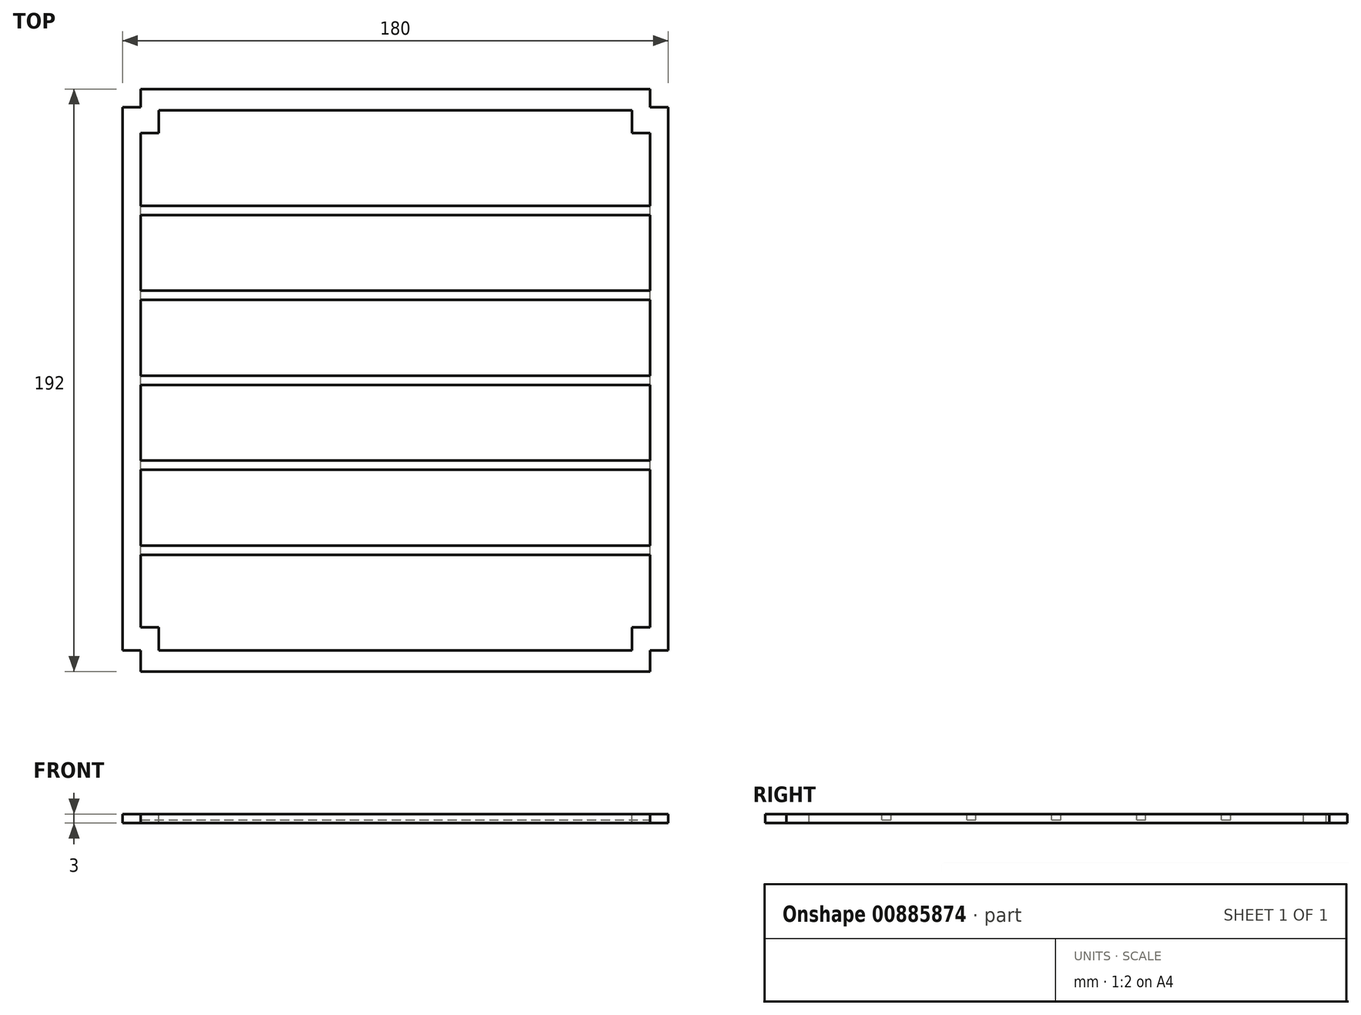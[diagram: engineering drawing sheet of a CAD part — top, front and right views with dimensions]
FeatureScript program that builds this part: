
annotation { "Feature Type Name" : "Feature", "Feature Type Description" : "" }
export const myFeature = defineFeature(function(context is Context, id is Id, definition is map)
    precondition{}
    {
        {
            var Q0;
            Q0=qCreatedBy(makeId("Top.planeOp"),FACE);
            var sketch = newSketch(context, id + "F0", { "sketchPlane" : qUnion([Q0])});
            skLineSegment(sketch, "E0.bottom", {"start": v(0, 0) * mm, "end": v(180, 0) * mm});
            skLineSegment(sketch, "E0.top", {"start": v(0, -190) * mm, "end": v(180, -190) * mm});
            skLineSegment(sketch, "E0.left", {"start": v(0, 0) * mm, "end": v(0, -190) * mm});
            skLineSegment(sketch, "E0.right", {"start": v(180, 0) * mm, "end": v(180, -190) * mm});
            skSolve(sketch);
        }
        {
            var Q0;
            Q0 = qSketchRegion(id + "F0", true);
            extrude(context, id + "F1", {"entities" : qUnion([Q0]), "depth" : 3 * mm, "offsetDistance" : 25 * mm});
        }
        {
            var Q0;
            Q0=makeQuery(id+"F1.opExtrude","CAP_FACE",FACE,{"disambiguationData":[OSD([sQuery(id+"F0.wireOp",EDGE,"E0.bottom"),sQuery(id+"F0.wireOp",EDGE,"E0.top"),sQuery(id+"F0.wireOp",EDGE,"E0.left"),sQuery(id+"F0.wireOp",EDGE,"E0.right")])],"isStart":false});
            var sketch = newSketch(context, id + "F2", { "sketchPlane" : qUnion([Q0])});
            skLineSegment(sketch, "E1.bottom", {"start": v(0, -190) * mm, "end": v(6, -190) * mm});
            skLineSegment(sketch, "E1.top", {"start": v(0, -184) * mm, "end": v(6, -184) * mm});
            skLineSegment(sketch, "E1.left", {"start": v(0, -190) * mm, "end": v(0, -184) * mm});
            skLineSegment(sketch, "E1.right", {"start": v(6, -190) * mm, "end": v(6, -184) * mm});
            skLineSegment(sketch, "E2.bottom", {"start": v(180, -190) * mm, "end": v(174, -190) * mm});
            skLineSegment(sketch, "E2.top", {"start": v(180, -184) * mm, "end": v(174, -184) * mm});
            skLineSegment(sketch, "E2.left", {"start": v(180, -190) * mm, "end": v(180, -184) * mm});
            skLineSegment(sketch, "E2.right", {"start": v(174, -190) * mm, "end": v(174, -184) * mm});
            skLineSegment(sketch, "E3.bottom", {"start": v(180, 0) * mm, "end": v(174, 0) * mm});
            skLineSegment(sketch, "E3.top", {"start": v(180, -6) * mm, "end": v(174, -6) * mm});
            skLineSegment(sketch, "E3.left", {"start": v(180, 0) * mm, "end": v(180, -6) * mm});
            skLineSegment(sketch, "E3.right", {"start": v(174, 0) * mm, "end": v(174, -6) * mm});
            skLineSegment(sketch, "E4.bottom", {"start": v(0, 0) * mm, "end": v(6, 0) * mm});
            skLineSegment(sketch, "E4.top", {"start": v(0, -6) * mm, "end": v(6, -6) * mm});
            skLineSegment(sketch, "E4.left", {"start": v(0, 0) * mm, "end": v(0, -6) * mm});
            skLineSegment(sketch, "E4.right", {"start": v(6, 0) * mm, "end": v(6, -6) * mm});
            skSolve(sketch);
        }
        {
            var Q0;
            Q0 = qSketchRegion(id + "F2", true);
            extrude(context, id + "F3", {"entities" : qUnion([Q0]), "operationType" : NewBodyOperationType.REMOVE, "endBound" : BoundingType.THROUGH_ALL, "oppositeDirection" : true, "depth" : 25 * mm, "offsetDistance" : 25 * mm});
        }
        {
            var Q0;
            Q0=makeQuery(id+"F1.opExtrude","CAP_FACE",FACE,{"disambiguationData":[OSD([sQuery(id+"F0.wireOp",EDGE,"E0.bottom"),sQuery(id+"F0.wireOp",EDGE,"E0.top"),sQuery(id+"F0.wireOp",EDGE,"E0.left"),sQuery(id+"F0.wireOp",EDGE,"E0.right")])],"isStart":false});
            var sketch = newSketch(context, id + "F4", { "sketchPlane" : qUnion([Q0])});
            skLineSegment(sketch, "E5.bottom", {"start": v(6, -176.5) * mm, "end": v(12, -176.5) * mm});
            skLineSegment(sketch, "E5.top", {"start": v(6, -152.5) * mm, "end": v(174, -152.5) * mm});
            skLineSegment(sketch, "E5.left", {"start": v(6, -176.5) * mm, "end": v(6, -152.5) * mm});
            skLineSegment(sketch, "E5.right", {"start": v(174, -176.5) * mm, "end": v(174, -152.5) * mm});
            skLineSegment(sketch, "E6.bottom", {"start": v(6, -149.5) * mm, "end": v(174, -149.5) * mm});
            skLineSegment(sketch, "E6.top", {"start": v(6, -124.5) * mm, "end": v(174, -124.5) * mm});
            skLineSegment(sketch, "E6.left", {"start": v(6, -149.5) * mm, "end": v(6, -124.5) * mm});
            skLineSegment(sketch, "E6.right", {"start": v(174, -149.5) * mm, "end": v(174, -124.5) * mm});
            skLineSegment(sketch, "E7.bottom", {"start": v(6, -121.5) * mm, "end": v(174, -121.5) * mm});
            skLineSegment(sketch, "E7.top", {"start": v(6, -96.5) * mm, "end": v(174, -96.5) * mm});
            skLineSegment(sketch, "E7.left", {"start": v(6, -121.5) * mm, "end": v(6, -96.5) * mm});
            skLineSegment(sketch, "E7.right", {"start": v(174, -121.5) * mm, "end": v(174, -96.5) * mm});
            skLineSegment(sketch, "E8.bottom", {"start": v(6, -93.5) * mm, "end": v(174, -93.5) * mm});
            skLineSegment(sketch, "E8.top", {"start": v(6, -68.5) * mm, "end": v(174, -68.5) * mm});
            skLineSegment(sketch, "E8.left", {"start": v(6, -93.5) * mm, "end": v(6, -68.5) * mm});
            skLineSegment(sketch, "E8.right", {"start": v(174, -93.5) * mm, "end": v(174, -68.5) * mm});
            skLineSegment(sketch, "E9.bottom", {"start": v(6, -65.5) * mm, "end": v(174, -65.5) * mm});
            skLineSegment(sketch, "E9.top", {"start": v(6, -40.5) * mm, "end": v(174, -40.5) * mm});
            skLineSegment(sketch, "E9.left", {"start": v(6, -65.5) * mm, "end": v(6, -40.5) * mm});
            skLineSegment(sketch, "E9.right", {"start": v(174, -65.5) * mm, "end": v(174, -40.5) * mm});
            skLineSegment(sketch, "E10.bottom", {"start": v(6, -37.5) * mm, "end": v(174, -37.5) * mm});
            skLineSegment(sketch, "E10.top", {"start": v(6, -13.5) * mm, "end": v(12, -13.5) * mm});
            skLineSegment(sketch, "E10.left", {"start": v(6, -37.5) * mm, "end": v(6, -13.5) * mm});
            skLineSegment(sketch, "E10.right", {"start": v(174, -37.5) * mm, "end": v(174, -13.5) * mm});
            skLineSegment(sketch, "E11.bottom", {"start": v(12, -184) * mm, "end": v(168, -184) * mm});
            skLineSegment(sketch, "E11.left", {"start": v(12, -184) * mm, "end": v(12, -176.5) * mm});
            skLineSegment(sketch, "E11.right", {"start": v(168, -184) * mm, "end": v(168, -176.5) * mm});
            skLineSegment(sketch, "E12.bottom", {"start": v(12, -6) * mm, "end": v(168, -6) * mm});
            skLineSegment(sketch, "E12.left", {"start": v(12, -6) * mm, "end": v(12, -13.5) * mm});
            skLineSegment(sketch, "E12.right", {"start": v(168, -6) * mm, "end": v(168, -13.5) * mm});
            skLineSegment(sketch, "E13.trimOffspring", {"start": v(168, -13.5) * mm, "end": v(174, -13.5) * mm});
            skLineSegment(sketch, "E14.trimOffspring", {"start": v(168, -176.5) * mm, "end": v(174, -176.5) * mm});
            skSolve(sketch);
        }
        {
            var Q0;
            Q0 = qSketchRegion(id + "F4", true);
            extrude(context, id + "F5", {"entities" : qUnion([Q0]), "operationType" : NewBodyOperationType.REMOVE, "endBound" : BoundingType.THROUGH_ALL, "oppositeDirection" : true, "depth" : 25 * mm, "offsetDistance" : 25 * mm});
        }
        {
            var Q0;
            Q0=makeQuery(id+"F1.opExtrude","SWEPT_FACE",FACE,{"disambiguationData":[OSD([sQuery(id+"F0.wireOp",EDGE,"E0.top")])]});
            extrude(context, id + "F6", {"entities" : qUnion([Q0]), "operationType" : NewBodyOperationType.ADD, "depth" : 1 * mm, "offsetDistance" : 25 * mm});
        }
        {
            var Q0;
            Q0=makeQuery(id+"F1.opExtrude","SWEPT_FACE",FACE,{"disambiguationData":[OSD([sQuery(id+"F0.wireOp",EDGE,"E0.bottom")])]});
            extrude(context, id + "F7", {"entities" : qUnion([Q0]), "operationType" : NewBodyOperationType.ADD, "depth" : 1 * mm, "offsetDistance" : 25 * mm});
        }
        {
            var Q0;
            Q0=makeQuery(id+"F3.boolean.opBoolean","COPY",FACE,{"derivedFrom":makeQuery(id+"F3.opExtrude","SWEPT_FACE",FACE,{"disambiguationData":[OSD([sQuery(id+"F2.wireOp",EDGE,"E3.top")])]})});
            var Q1;
            Q1=makeQuery(id+"F3.boolean.opBoolean","COPY",FACE,{"derivedFrom":makeQuery(id+"F3.opExtrude","SWEPT_FACE",FACE,{"disambiguationData":[OSD([sQuery(id+"F2.wireOp",EDGE,"E4.top")])]})});
            var Q2;
            Q2=makeQuery(id+"F3.boolean.opBoolean","COPY",FACE,{"derivedFrom":makeQuery(id+"F3.opExtrude","SWEPT_FACE",FACE,{"disambiguationData":[OSD([sQuery(id+"F2.wireOp",EDGE,"E1.top")])]})});
            var Q3;
            Q3=makeQuery(id+"F3.boolean.opBoolean","COPY",FACE,{"derivedFrom":makeQuery(id+"F3.opExtrude","SWEPT_FACE",FACE,{"disambiguationData":[OSD([sQuery(id+"F2.wireOp",EDGE,"E2.top")])]})});
            extrude(context, id + "F8", {"entities" : qUnion([Q0, Q1, Q2, Q3]), "operationType" : NewBodyOperationType.ADD, "depth" : 1 * mm, "offsetDistance" : 25 * mm});
        }
        {
            var Q0;
            {var subQ0=sQuery(id+"F0.wireOp",EDGE,"E0.right");var subQ1=sQuery(id+"F0.wireOp",EDGE,"E0.left");var subQ2=sQuery(id+"F0.wireOp",EDGE,"E0.top");var subQ3=sQuery(id+"F0.wireOp",EDGE,"E0.bottom");Q0=makeQuery(id+"F8.boolean.opBoolean","MERGE",FACE,{"derivedFrom":[makeQuery(id+"F7.boolean.opBoolean","MERGE",FACE,{"derivedFrom":[makeQuery(id+"F6.boolean.opBoolean","MERGE",FACE,{"derivedFrom":[makeQuery(id+"F1.opExtrude","CAP_FACE",FACE,{"disambiguationData":[OSD([subQ3,subQ2,subQ1,subQ0])],"isStart":true}),makeQuery(id+"F6.opExtrude","SWEPT_FACE",FACE,{"disambiguationData":[OSD([subQ2]),TDD([makeQuery(id+"F1.opExtrude","CAP_EDGE",EDGE,{"disambiguationData":[OSD([subQ2])],"isStart":true})])]})]}),makeQuery(id+"F7.opExtrude","SWEPT_FACE",FACE,{"disambiguationData":[OSD([subQ3]),TDD([makeQuery(id+"F1.opExtrude","CAP_EDGE",EDGE,{"disambiguationData":[OSD([subQ3])],"isStart":true})])]})]}),makeQuery(id+"F8.opExtrude","SWEPT_FACE",FACE,{"disambiguationData":[OSD([subQ3,subQ2,subQ1,subQ0,sQuery(id+"F2.wireOp",EDGE,"E3.top")])]}),makeQuery(id+"F8.opExtrude","SWEPT_FACE",FACE,{"disambiguationData":[OSD([subQ3,subQ2,subQ1,subQ0,sQuery(id+"F2.wireOp",EDGE,"E4.top")])]})]});}
            var sketch = newSketch(context, id + "F9", { "sketchPlane" : qUnion([Q0])});
            skLineSegment(sketch, "E15.bottom", {"start": v(6, 159.69) * mm, "end": v(174, 159.69) * mm});
            skLineSegment(sketch, "E15.top", {"start": v(6, 25.5) * mm, "end": v(174, 25.5) * mm});
            skLineSegment(sketch, "E15.left", {"start": v(6, 159.69) * mm, "end": v(6, 25.5) * mm});
            skLineSegment(sketch, "E15.right", {"start": v(174, 159.69) * mm, "end": v(174, 25.5) * mm});
            skSolve(sketch);
        }
        {
            var Q0;
            Q0 = qSketchRegion(id + "F9", true);
            extrude(context, id + "F10", {"entities" : qUnion([Q0]), "operationType" : NewBodyOperationType.REMOVE, "oppositeDirection" : true, "depth" : 1 * mm, "offsetDistance" : 25 * mm});
        }
    });
